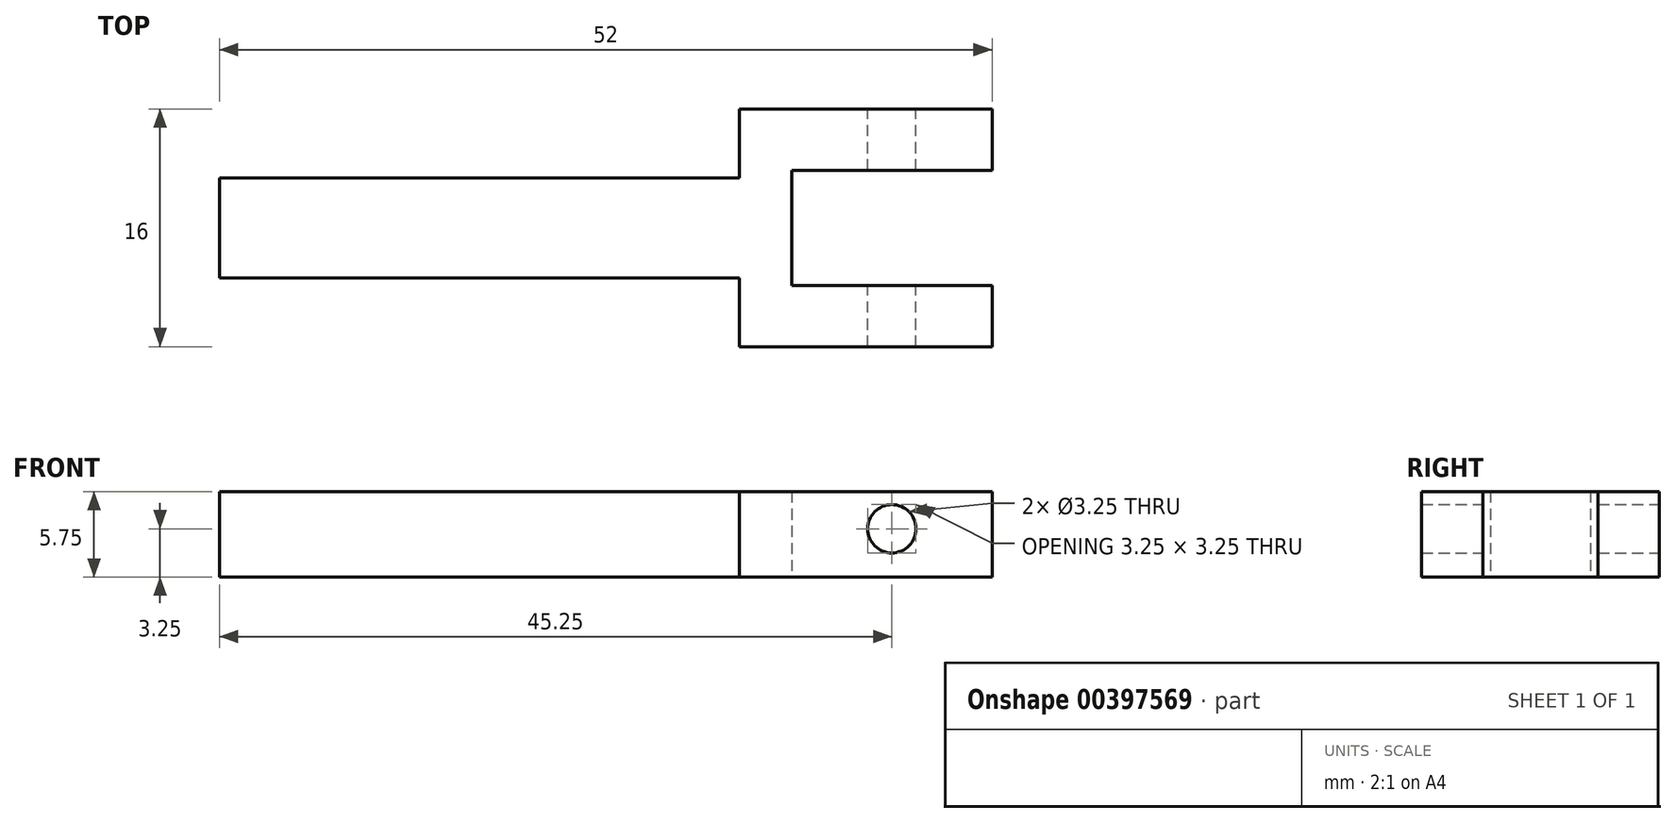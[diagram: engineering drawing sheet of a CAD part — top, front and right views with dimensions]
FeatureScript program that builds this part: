
annotation { "Feature Type Name" : "Feature", "Feature Type Description" : "" }
export const myFeature = defineFeature(function(context is Context, id is Id, definition is map)
    precondition{}
    {
        {
            var Q0;
            Q0=qCreatedBy(makeId("Top.planeOp"),FACE);
            var sketch = newSketch(context, id + "F0", { "sketchPlane" : qUnion([Q0])});
            skLineSegment(sketch, "E0.bottom", {"start": v(-35, 3.38) * mm, "end": v(0, 3.38) * mm});
            skLineSegment(sketch, "E0.top", {"start": v(-35, -3.37) * mm, "end": v(0, -3.37) * mm});
            skLineSegment(sketch, "E0.left", {"start": v(-35, 3.38) * mm, "end": v(-35, -3.37) * mm});
            skLineSegment(sketch, "E1", {"start": v(0, 3.38) * mm, "end": v(0, 8) * mm});
            skLineSegment(sketch, "E2", {"start": v(0, 8) * mm, "end": v(17, 8) * mm});
            skLineSegment(sketch, "E3", {"start": v(17, 8) * mm, "end": v(17, 3.88) * mm});
            skLineSegment(sketch, "E4", {"start": v(17, -8) * mm, "end": v(0, -8) * mm});
            skLineSegment(sketch, "E5", {"start": v(0, -8) * mm, "end": v(0, -3.37) * mm});
            skLineSegment(sketch, "E6", {"start": v(17, 3.88) * mm, "end": v(3.5, 3.87) * mm});
            skLineSegment(sketch, "E7", {"start": v(3.5, 3.87) * mm, "end": v(3.5, -3.87) * mm});
            skLineSegment(sketch, "E8", {"start": v(3.5, -3.87) * mm, "end": v(17, -3.87) * mm});
            skLineSegment(sketch, "E9.trimOffspring", {"start": v(17, -3.87) * mm, "end": v(17, -8) * mm});
            skSolve(sketch);
        }
        {
            var Q0;
            Q0 = qSketchRegion(id + "F0", true);
            extrude(context, id + "F1", {"entities" : qUnion([Q0]), "depth" : 5.75 * mm});
        }
        {
            var Q0;
            Q0=qCreatedBy(makeId("Front.planeOp"),FACE);
            var sketch = newSketch(context, id + "F2", { "sketchPlane" : qUnion([Q0])});
            skCircle(sketch, "E10", {"center": v(10.25, 3.25) * mm, "radius": 1.63 * mm});
            skSolve(sketch);
        }
        {
            var Q0;
            Q0 = qSketchRegion(id + "F2", true);
            extrude(context, id + "F3", {"entities" : qUnion([Q0]), "operationType" : NewBodyOperationType.REMOVE, "endBound" : BoundingType.SYMMETRIC, "depth" : 25 * mm});
        }
    });
